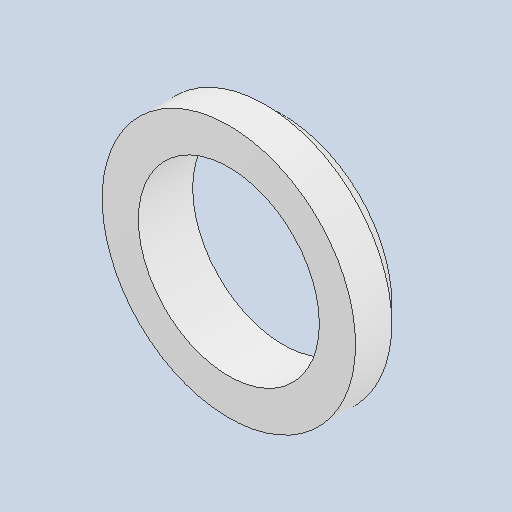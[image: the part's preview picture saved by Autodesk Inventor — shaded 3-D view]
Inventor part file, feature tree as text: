
AUTODESK INVENTOR PART (.ipt)
format: ipt  version: 2023 (Build 270158030, 158C)  size: 106,496 bytes
history: native  units: mm
features: extrude x1, chamfer x1, sketch x1
ambient origin geometry x8: Origin, YZ Plane, XZ Plane, XY Plane, X Axis, Y Axis, Z Axis, Center Point
bodies: Solid1 (feature_tree)
feature tree (3):
  extrude  "Extrusion1"  Depth=1.5mm
  chamfer  "Chamfer1"  Distance=1.5mm
  sketch  "Sketch1"  dims[d0=5.0mm d1=7.0mm d2=1.5mm d3=0.0mm d4=0.5mm d5=2.0mm d6=45.0deg]
